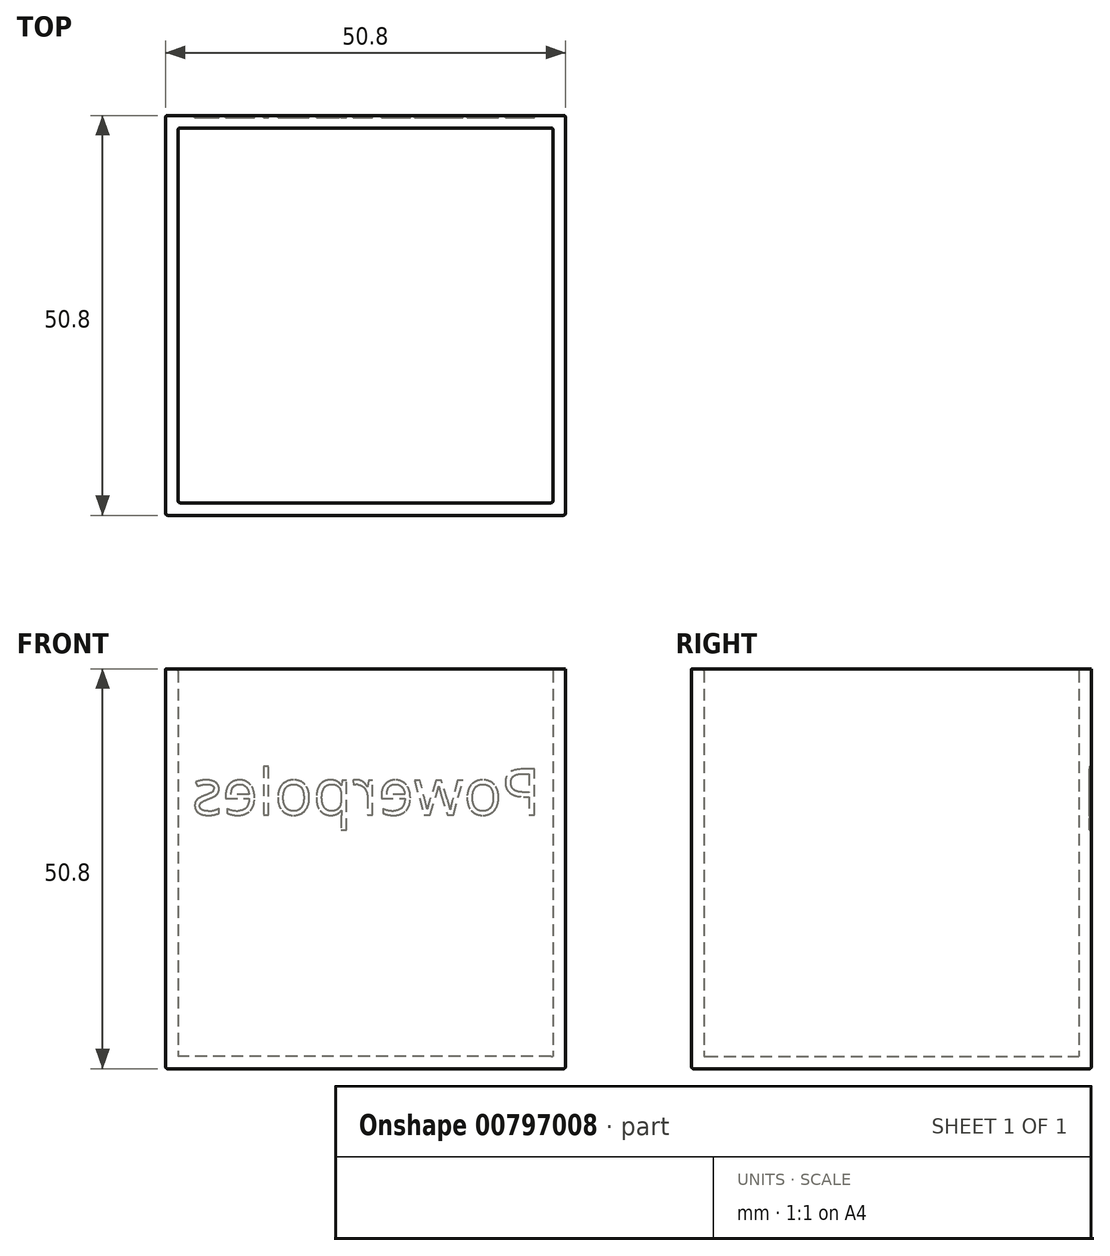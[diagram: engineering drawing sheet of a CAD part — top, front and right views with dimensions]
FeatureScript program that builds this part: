
annotation { "Feature Type Name" : "Feature", "Feature Type Description" : "" }
export const myFeature = defineFeature(function(context is Context, id is Id, definition is map)
    precondition{}
    {
        {
            var Q0;
            Q0=qCreatedBy(makeId("Top.planeOp"),FACE);
            var sketch = newSketch(context, id + "F0", { "sketchPlane" : qUnion([Q0])});
            skLineSegment(sketch, "E0.bottom", {"start": v(25.4, -25.4) * mm, "end": v(-25.4, -25.4) * mm});
            skLineSegment(sketch, "E0.top", {"start": v(25.4, 25.4) * mm, "end": v(-25.4, 25.4) * mm});
            skLineSegment(sketch, "E0.left", {"start": v(25.4, -25.4) * mm, "end": v(25.4, 25.4) * mm});
            skLineSegment(sketch, "E0.right", {"start": v(-25.4, -25.4) * mm, "end": v(-25.4, 25.4) * mm});
            skPoint(sketch, "E0.middle", {"position": v(0, 0) * mm});
            skSolve(sketch);
        }
        {
            var Q0;
            Q0=qSketchRegion(id+"F0",true);
            extrude(context, id + "F1", {"entities" : qUnion([Q0]), "depth" : 1.59 * mm, "offsetDistance" : 25.4 * mm});
        }
        {
            var Q0;
            Q0=makeQuery(id+"F1.opExtrude","CAP_FACE",FACE,{"disambiguationData":[OSD([sQuery(id+"F0.wireOp",EDGE,"E0.bottom"),sQuery(id+"F0.wireOp",EDGE,"E0.top"),sQuery(id+"F0.wireOp",EDGE,"E0.left"),sQuery(id+"F0.wireOp",EDGE,"E0.right")])],"isStart":false});
            var sketch = newSketch(context, id + "F2", { "sketchPlane" : qUnion([Q0])});
            skLineSegment(sketch, "E1.bottom", {"start": v(25.4, -25.4) * mm, "end": v(-25.4, -25.4) * mm});
            skLineSegment(sketch, "E1.top", {"start": v(25.4, 25.4) * mm, "end": v(-25.4, 25.4) * mm});
            skLineSegment(sketch, "E1.left", {"start": v(25.4, -25.4) * mm, "end": v(25.4, 25.4) * mm});
            skLineSegment(sketch, "E1.right", {"start": v(-25.4, -25.4) * mm, "end": v(-25.4, 25.4) * mm});
            skPoint(sketch, "E1.middle", {"position": v(0, 0) * mm});
            skLineSegment(sketch, "E2.0", {"start": v(23.81, 23.81) * mm, "end": v(-23.81, 23.81) * mm});
            skLineSegment(sketch, "E2.1", {"start": v(23.81, -23.81) * mm, "end": v(23.81, 23.81) * mm});
            skLineSegment(sketch, "E2.2", {"start": v(23.81, -23.81) * mm, "end": v(-23.81, -23.81) * mm});
            skLineSegment(sketch, "E2.3", {"start": v(-23.81, -23.81) * mm, "end": v(-23.81, 23.81) * mm});
            skSolve(sketch);
        }
        {
            var Q0;
            Q0=qSketchRegion(id+"F2",true);
            extrude(context, id + "F3", {"entities" : qUnion([Q0]), "operationType" : NewBodyOperationType.ADD, "depth" : 49.2 * mm, "offsetDistance" : 25.4 * mm});
        }
        {
            var Q0;
            Q0=makeQuery(id+"F3.opExtrude","CAP_EDGE",EDGE,{"disambiguationData":[OSD([sQuery(id+"F2.wireOp",EDGE,"E2.3")])],"isStart":true});
            var Q1;
            Q1=makeQuery(id+"F3.opExtrude","SWEPT_EDGE",EDGE,{"disambiguationData":[OSD([sQuery(id+"F2.wireOp",EDGE,"E2.2"),sQuery(id+"F2.wireOp",EDGE,"E2.3")])]});
            var Q2;
            Q2=makeQuery(id+"F3.opExtrude","CAP_EDGE",EDGE,{"disambiguationData":[OSD([sQuery(id+"F2.wireOp",EDGE,"E2.2")])],"isStart":true});
            var Q3;
            Q3=makeQuery(id+"F3.opExtrude","CAP_EDGE",EDGE,{"disambiguationData":[OSD([sQuery(id+"F2.wireOp",EDGE,"E2.3")])],"isStart":false});
            var Q4;
            Q4=makeQuery(id+"F3.opExtrude","CAP_EDGE",EDGE,{"disambiguationData":[OSD([sQuery(id+"F2.wireOp",EDGE,"E2.2")])],"isStart":false});
            var Q5;
            Q5=makeQuery(id+"F3.opExtrude","CAP_EDGE",EDGE,{"disambiguationData":[OSD([sQuery(id+"F2.wireOp",EDGE,"E2.0")])],"isStart":true});
            var Q6;
            Q6=makeQuery(id+"F3.opExtrude","SWEPT_EDGE",EDGE,{"disambiguationData":[OSD([sQuery(id+"F2.wireOp",EDGE,"E2.0"),sQuery(id+"F2.wireOp",EDGE,"E2.3")])]});
            var Q7;
            Q7=makeQuery(id+"F3.opExtrude","CAP_EDGE",EDGE,{"disambiguationData":[OSD([sQuery(id+"F2.wireOp",EDGE,"E2.0")])],"isStart":false});
            var Q8;
            Q8=makeQuery(id+"F3.opExtrude","SWEPT_EDGE",EDGE,{"disambiguationData":[OSD([sQuery(id+"F2.wireOp",EDGE,"E2.0"),sQuery(id+"F2.wireOp",EDGE,"E2.1")])]});
            var Q9;
            Q9=makeQuery(id+"F3.opExtrude","CAP_EDGE",EDGE,{"disambiguationData":[OSD([sQuery(id+"F2.wireOp",EDGE,"E2.1")])],"isStart":true});
            var Q10;
            Q10=makeQuery(id+"F3.opExtrude","CAP_EDGE",EDGE,{"disambiguationData":[OSD([sQuery(id+"F2.wireOp",EDGE,"E2.1")])],"isStart":false});
            var Q11;
            Q11=makeQuery(id+"F3.opExtrude","SWEPT_EDGE",EDGE,{"disambiguationData":[OSD([sQuery(id+"F2.wireOp",EDGE,"E2.1"),sQuery(id+"F2.wireOp",EDGE,"E2.2")])]});
            var Q12;
            Q12=makeQuery(id+"F3.boolean.opBoolean","MERGE",EDGE,{"derivedFrom":[makeQuery(id+"F1.opExtrude","SWEPT_EDGE",EDGE,{"disambiguationData":[OSD([sQuery(id+"F0.wireOp",EDGE,"E0.bottom"),sQuery(id+"F0.wireOp",EDGE,"E0.right")])]}),makeQuery(id+"F3.opExtrude","SWEPT_EDGE",EDGE,{"disambiguationData":[OSD([sQuery(id+"F2.wireOp",EDGE,"E1.bottom"),sQuery(id+"F2.wireOp",EDGE,"E1.right")])]})]});
            var Q13;
            Q13=makeQuery(id+"F3.boolean.opBoolean","MERGE",EDGE,{"derivedFrom":[makeQuery(id+"F1.opExtrude","SWEPT_EDGE",EDGE,{"disambiguationData":[OSD([sQuery(id+"F0.wireOp",EDGE,"E0.bottom"),sQuery(id+"F0.wireOp",EDGE,"E0.left")])]}),makeQuery(id+"F3.opExtrude","SWEPT_EDGE",EDGE,{"disambiguationData":[OSD([sQuery(id+"F2.wireOp",EDGE,"E1.bottom"),sQuery(id+"F2.wireOp",EDGE,"E1.left")])]})]});
            var Q14;
            Q14=makeQuery(id+"F3.boolean.opBoolean","MERGE",EDGE,{"derivedFrom":[makeQuery(id+"F1.opExtrude","SWEPT_EDGE",EDGE,{"disambiguationData":[OSD([sQuery(id+"F0.wireOp",EDGE,"E0.top"),sQuery(id+"F0.wireOp",EDGE,"E0.left")])]}),makeQuery(id+"F3.opExtrude","SWEPT_EDGE",EDGE,{"disambiguationData":[OSD([sQuery(id+"F2.wireOp",EDGE,"E1.top"),sQuery(id+"F2.wireOp",EDGE,"E1.left")])]})]});
            var Q15;
            Q15=makeQuery(id+"F3.boolean.opBoolean","MERGE",EDGE,{"derivedFrom":[makeQuery(id+"F1.opExtrude","SWEPT_EDGE",EDGE,{"disambiguationData":[OSD([sQuery(id+"F0.wireOp",EDGE,"E0.top"),sQuery(id+"F0.wireOp",EDGE,"E0.right")])]}),makeQuery(id+"F3.opExtrude","SWEPT_EDGE",EDGE,{"disambiguationData":[OSD([sQuery(id+"F2.wireOp",EDGE,"E1.top"),sQuery(id+"F2.wireOp",EDGE,"E1.right")])]})]});
            var Q16;
            Q16=makeQuery(id+"F1.opExtrude","CAP_EDGE",EDGE,{"disambiguationData":[OSD([sQuery(id+"F0.wireOp",EDGE,"E0.right")])],"isStart":true});
            var Q17;
            Q17=makeQuery(id+"F1.opExtrude","CAP_EDGE",EDGE,{"disambiguationData":[OSD([sQuery(id+"F0.wireOp",EDGE,"E0.bottom")])],"isStart":true});
            var Q18;
            Q18=makeQuery(id+"F1.opExtrude","CAP_EDGE",EDGE,{"disambiguationData":[OSD([sQuery(id+"F0.wireOp",EDGE,"E0.top")])],"isStart":true});
            var Q19;
            Q19=makeQuery(id+"F1.opExtrude","CAP_EDGE",EDGE,{"disambiguationData":[OSD([sQuery(id+"F0.wireOp",EDGE,"E0.left")])],"isStart":true});
            fillet(context, id + "F4", {"entities" : qUnion([Q0, Q1, Q2, Q3, Q4, Q5, Q6, Q7, Q8, Q9, Q10, Q11, Q12, Q13, Q14, Q15, Q16, Q17, Q18, Q19]), "radius" : 0.25 * mm, "tangentPropagation" : true, "allowEdgeOverflow" : false});
        }
        {
            var Q0;
            Q0=makeQuery(id+"F3.boolean.opBoolean","MERGE",FACE,{"derivedFrom":[makeQuery(id+"F1.opExtrude","SWEPT_FACE",FACE,{"disambiguationData":[OSD([sQuery(id+"F0.wireOp",EDGE,"E0.top")])]}),makeQuery(id+"F3.opExtrude","SWEPT_FACE",FACE,{"disambiguationData":[OSD([sQuery(id+"F2.wireOp",EDGE,"E1.top")])]})]});
            var sketch = newSketch(context, id + "F5", { "sketchPlane" : qUnion([Q0])});
            skText(sketch, "E3", { "text": "Powerpoles", "fontName": "OpenSans-Regular.ttf"});
            const initialGuessF5  = {"E3": [-0.02223, 0.03226, 1, 0, 0.00584]};
            skSetInitialGuess(sketch, initialGuessF5);
            skSolve(sketch);
        }
        {
            var Q0;
            Q0 = qSketchRegion(id + "F5", true);
            extrude(context, id + "F6", {"entities" : qUnion([Q0]), "operationType" : NewBodyOperationType.REMOVE, "oppositeDirection" : true, "depth" : 0.25 * mm, "offsetDistance" : 25.4 * mm});
        }
    });
